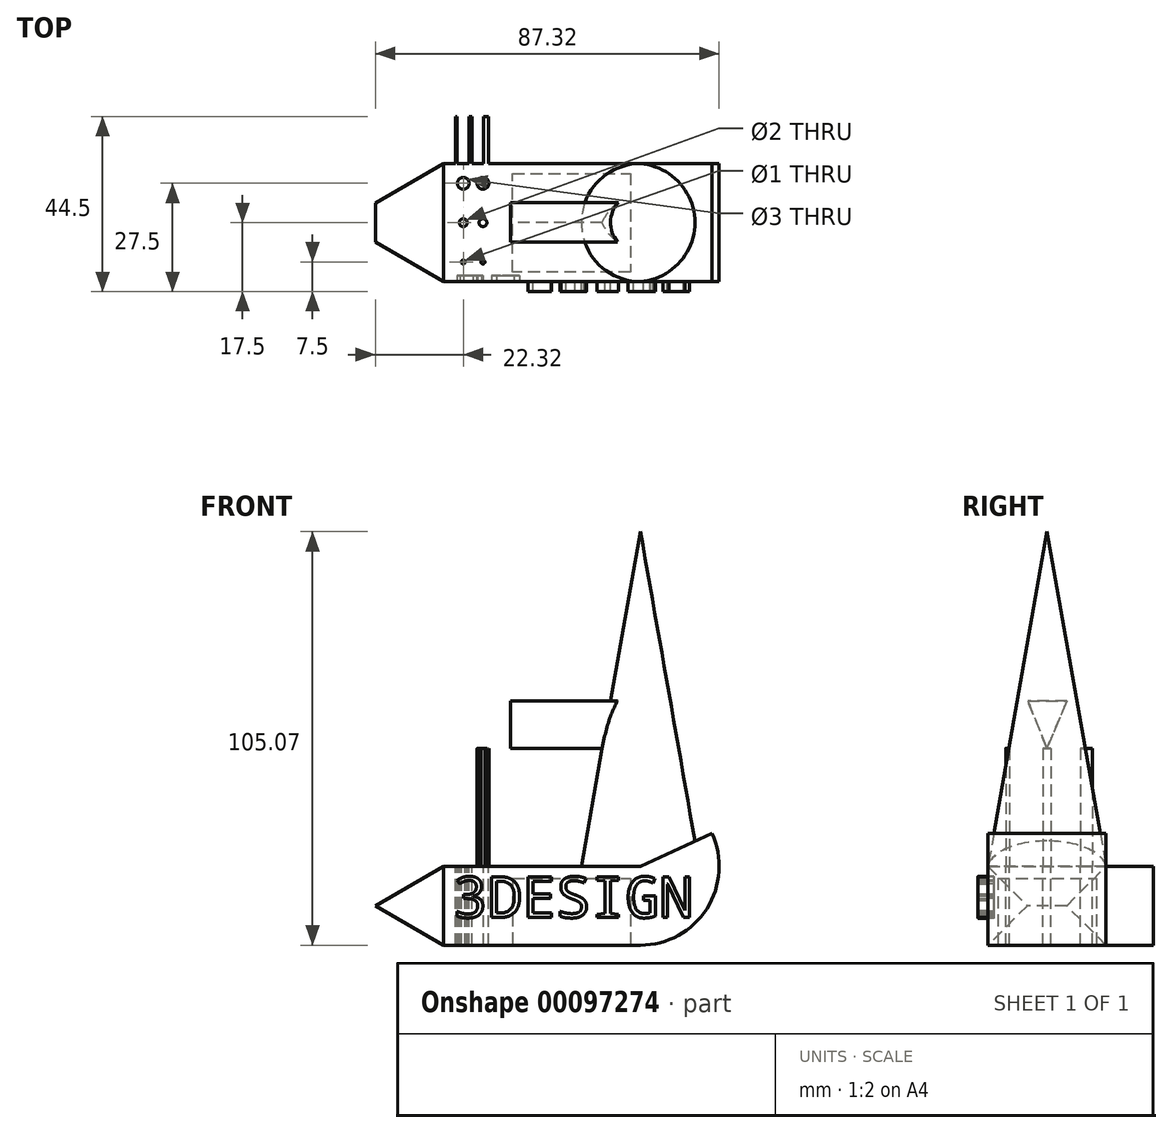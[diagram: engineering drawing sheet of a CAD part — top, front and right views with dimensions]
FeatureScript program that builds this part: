
annotation { "Feature Type Name" : "Feature", "Feature Type Description" : "" }
export const myFeature = defineFeature(function(context is Context, id is Id, definition is map)
    precondition{}
    {
        {
            var Q0;
            Q0=qCreatedBy(makeId("Top.planeOp"),FACE);
            var sketch = newSketch(context, id + "F0", { "sketchPlane" : qUnion([Q0])});
            skLineSegment(sketch, "E0.bottom", {"start": v(25, -15) * mm, "end": v(-25, -15) * mm});
            skLineSegment(sketch, "E0.top", {"start": v(25, 15) * mm, "end": v(-25, 15) * mm});
            skLineSegment(sketch, "E0.left", {"start": v(25, -15) * mm, "end": v(25, 15) * mm});
            skLineSegment(sketch, "E0.right", {"start": v(-25, -15) * mm, "end": v(-25, 15) * mm});
            skPoint(sketch, "E0.middle", {"position": v(0, 0) * mm});
            skSolve(sketch);
        }
        {
            var Q0;
            Q0=makeQuery(id+"F0.imprint","IMPRINT",FACE,{"disambiguationData":[TD([[makeQuery(id+"F0.imprint","IMPRINT",EDGE,{"derivedFrom":sQuery(id+"F0.wireOp",EDGE,"E0.bottom")}),-1.0]])]});
            extrude(context, id + "F1", {"entities" : qUnion([Q0]), "depth" : 20 * mm});
        }
        {
            var Q0;
            Q0=makeQuery(id+"F1.opExtrude","SWEPT_FACE",FACE,{"disambiguationData":[OSD([sQuery(id+"F0.wireOp",EDGE,"E0.bottom")])]});
            var sketch = newSketch(context, id + "F2", { "sketchPlane" : qUnion([Q0])});
            skPoint(sketch, "E1", {"position": v(25, 0) * mm});
            skPoint(sketch, "E2", {"position": v(25, 20) * mm});
            skLineSegment(sketch, "E3", {"start": v(25, 0) * mm, "end": v(25, 20) * mm});
            skLineSegment(sketch, "E4", {"start": v(25, 20) * mm, "end": v(43.13, 28.45) * mm});
            skArc(sketch, "E5", {"start": v(25, 0) * mm, "mid": v(41.87, 9.25) * mm, "end": v(43.13, 28.45) * mm});
            skSolve(sketch);
        }
        {
            var Q0;
            Q0 = qSketchRegion(id + "F2", true);
            var Q1;
            Q1=makeQuery(id+"F1.opExtrude","SWEPT_FACE",FACE,{"disambiguationData":[OSD([sQuery(id+"F0.wireOp",EDGE,"E0.top")])]});
            extrude(context, id + "F3", {"entities" : qUnion([Q0]), "operationType" : NewBodyOperationType.ADD, "endBound" : BoundingType.UP_TO_SURFACE, "oppositeDirection" : true, "endBoundEntityFace" : qUnion([Q1]), "depth" : 25 * mm});
        }
        {
            var Q0;
            Q0=makeQuery(id+"F1.opExtrude","SWEPT_FACE",FACE,{"disambiguationData":[OSD([sQuery(id+"F0.wireOp",EDGE,"E0.right")])]});
            extrude(context, id + "F4", {"entities" : qUnion([Q0]), "operationType" : NewBodyOperationType.ADD, "depth" : 25 * mm, "hasDraft" : true, "draftAngle" : 30 * degree, "draftPullDirection" : true});
        }
        {
            var Q0;
            Q0=makeQuery(id+"F1.opExtrude","CAP_FACE",FACE,{"disambiguationData":[OSD([sQuery(id+"F0.wireOp",EDGE,"E0.bottom"),sQuery(id+"F0.wireOp",EDGE,"E0.top"),sQuery(id+"F0.wireOp",EDGE,"E0.left"),sQuery(id+"F0.wireOp",EDGE,"E0.right")])],"isStart":false});
            var sketch = newSketch(context, id + "F5", { "sketchPlane" : qUnion([Q0])});
            skLineSegment(sketch, "E6", {"start": v(25, 15) * mm, "end": v(25, -15) * mm});
            skCircle(sketch, "E7", {"center": v(25, 0) * mm, "radius": 15 * mm});
            skSolve(sketch);
        }
        {
            var Q0;
            Q0 = qSketchRegion(id + "F5", true);
            extrude(context, id + "F6", {"entities" : qUnion([Q0]), "operationType" : NewBodyOperationType.ADD, "depth" : 90 * mm, "hasDraft" : true, "draftAngle" : 10 * degree, "draftPullDirection" : true});
        }
        {
            var Q0;
            Q0=qCreatedBy(makeId("Right.planeOp"),FACE);
            var sketch = newSketch(context, id + "F7", { "sketchPlane" : qUnion([Q0])});
            skLineSegment(sketch, "E8", {"start": v(0, 20) * mm, "end": v(0, 50) * mm});
            skLineSegment(sketch, "E9", {"start": v(0, 50) * mm, "end": v(-4.88, 62.07) * mm});
            skLineSegment(sketch, "E10", {"start": v(-4.88, 62.07) * mm, "end": v(5.12, 62.07) * mm});
            skLineSegment(sketch, "E11", {"start": v(5.12, 62.07) * mm, "end": v(0, 50) * mm});
            skSolve(sketch);
        }
        {
            var Q0;
            Q0=makeQuery(id+"F7.imprint","IMPRINT",FACE,{"disambiguationData":[TD([[makeQuery(id+"F7.imprint","IMPRINT",EDGE,{"derivedFrom":sQuery(id+"F7.wireOp",EDGE,"E9")}),-1.0]])]});
            extrude(context, id + "F8", {"entities" : qUnion([Q0]), "operationType" : NewBodyOperationType.ADD, "depth" : 25 * mm, "hasSecondDirection" : true, "secondDirectionOppositeDirection" : true, "secondDirectionDepth" : 8 * mm});
        }
        {
            var Q0;
            Q0=makeQuery(id+"F1.opExtrude","CAP_FACE",FACE,{"disambiguationData":[OSD([sQuery(id+"F0.wireOp",EDGE,"E0.bottom"),sQuery(id+"F0.wireOp",EDGE,"E0.top"),sQuery(id+"F0.wireOp",EDGE,"E0.left"),sQuery(id+"F0.wireOp",EDGE,"E0.right")])],"isStart":false});
            var sketch = newSketch(context, id + "F9", { "sketchPlane" : qUnion([Q0])});
            skLineSegment(sketch, "E12", {"start": v(-25, 0) * mm, "end": v(-15, 0) * mm});
            skPoint(sketch, "E12.endSnap0", {"position": v(-25, 0) * mm});
            skCircle(sketch, "E13", {"center": v(-15, 0) * mm, "radius": 1 * mm});
            skCircle(sketch, "E14", {"center": v(-15, -10) * mm, "radius": 0.5 * mm});
            skCircle(sketch, "E15", {"center": v(-15, 10) * mm, "radius": 1.5 * mm});
            skSolve(sketch);
        }
        {
            var Q0;
            Q0 = qSketchRegion(id + "F9", true);
            extrude(context, id + "F10", {"entities" : qUnion([Q0]), "operationType" : NewBodyOperationType.ADD, "depth" : 30 * mm});
        }
        {
            var Q0;
            Q0=makeQuery(id+"F1.opExtrude","CAP_FACE",FACE,{"disambiguationData":[OSD([sQuery(id+"F0.wireOp",EDGE,"E0.bottom"),sQuery(id+"F0.wireOp",EDGE,"E0.top"),sQuery(id+"F0.wireOp",EDGE,"E0.left"),sQuery(id+"F0.wireOp",EDGE,"E0.right")])],"isStart":false});
            var sketch = newSketch(context, id + "F11", { "sketchPlane" : qUnion([Q0])});
            skLineSegment(sketch, "E16", {"start": v(-25, 0) * mm, "end": v(-20, 0) * mm});
            skPoint(sketch, "E16.endSnap0", {"position": v(-25, 0) * mm});
            skCircle(sketch, "E17", {"center": v(-20, 0) * mm, "radius": 1 * mm});
            skCircle(sketch, "E18", {"center": v(-20, -10) * mm, "radius": 0.5 * mm});
            skCircle(sketch, "E19", {"center": v(-20, 10) * mm, "radius": 1.5 * mm});
            skSolve(sketch);
        }
        {
            var Q0;
            Q0 = qSketchRegion(id + "F11", true);
            extrude(context, id + "F12", {"entities" : qUnion([Q0]), "operationType" : NewBodyOperationType.REMOVE, "endBound" : BoundingType.THROUGH_ALL, "oppositeDirection" : true, "depth" : 25 * mm});
        }
        {
            var Q0;
            Q0=makeQuery(id+"F1.opExtrude","CAP_FACE",FACE,{"disambiguationData":[OSD([sQuery(id+"F0.wireOp",EDGE,"E0.bottom"),sQuery(id+"F0.wireOp",EDGE,"E0.top"),sQuery(id+"F0.wireOp",EDGE,"E0.left"),sQuery(id+"F0.wireOp",EDGE,"E0.right")])],"isStart":false});
            var sketch = newSketch(context, id + "F13", { "sketchPlane" : qUnion([Q0])});
            skLineSegment(sketch, "E20", {"start": v(-25, 15) * mm, "end": v(-22, 15) * mm});
            skLineSegment(sketch, "E21", {"start": v(-22, 15) * mm, "end": v(-22, 27) * mm});
            skLineSegment(sketch, "E22", {"start": v(-22, 27) * mm, "end": v(-21.6, 27) * mm});
            skLineSegment(sketch, "E23", {"start": v(-21.6, 27) * mm, "end": v(-21.6, 15) * mm});
            skLineSegment(sketch, "E24", {"start": v(-21.6, 15) * mm, "end": v(-22, 15) * mm});
            skLineSegment(sketch, "E25", {"start": v(-21.6, 15) * mm, "end": v(-18.6, 15) * mm});
            skLineSegment(sketch, "E26", {"start": v(-18.6, 15) * mm, "end": v(-18.6, 27) * mm});
            skLineSegment(sketch, "E27", {"start": v(-18.6, 27) * mm, "end": v(-17.8, 27) * mm});
            skLineSegment(sketch, "E28", {"start": v(-17.8, 27) * mm, "end": v(-17.8, 15) * mm});
            skLineSegment(sketch, "E29", {"start": v(-17.8, 15) * mm, "end": v(-18.6, 15) * mm});
            skLineSegment(sketch, "E30", {"start": v(-17.8, 15) * mm, "end": v(-14.8, 15) * mm});
            skLineSegment(sketch, "E31", {"start": v(-14.8, 15) * mm, "end": v(-14.8, 27) * mm});
            skLineSegment(sketch, "E32", {"start": v(-14.8, 27) * mm, "end": v(-13.6, 27) * mm});
            skLineSegment(sketch, "E33", {"start": v(-13.6, 27) * mm, "end": v(-13.6, 15) * mm});
            skLineSegment(sketch, "E34", {"start": v(-13.6, 15) * mm, "end": v(-14.8, 15) * mm});
            skSolve(sketch);
        }
        {
            var Q0;
            Q0 = qSketchRegion(id + "F13", true);
            extrude(context, id + "F14", {"entities" : qUnion([Q0]), "operationType" : NewBodyOperationType.ADD, "oppositeDirection" : true, "depth" : 20 * mm});
        }
        {
            var Q0;
            Q0=makeQuery(id+"F14.boolean.opBoolean","MERGE",FACE,{"derivedFrom":[makeQuery(id+"F1.opExtrude","CAP_FACE",FACE,{"disambiguationData":[OSD([sQuery(id+"F0.wireOp",EDGE,"E0.bottom"),sQuery(id+"F0.wireOp",EDGE,"E0.top"),sQuery(id+"F0.wireOp",EDGE,"E0.left"),sQuery(id+"F0.wireOp",EDGE,"E0.right")])],"isStart":true}),makeQuery(id+"F14.opExtrude","CAP_FACE",FACE,{"disambiguationData":[OSD([sQuery(id+"F13.wireOp",EDGE,"E21"),sQuery(id+"F13.wireOp",EDGE,"E22"),sQuery(id+"F13.wireOp",EDGE,"E23"),sQuery(id+"F13.wireOp",EDGE,"E24")])],"isStart":false}),makeQuery(id+"F14.opExtrude","CAP_FACE",FACE,{"disambiguationData":[OSD([sQuery(id+"F13.wireOp",EDGE,"E26"),sQuery(id+"F13.wireOp",EDGE,"E27"),sQuery(id+"F13.wireOp",EDGE,"E28"),sQuery(id+"F13.wireOp",EDGE,"E29")])],"isStart":false}),makeQuery(id+"F14.opExtrude","CAP_FACE",FACE,{"disambiguationData":[OSD([sQuery(id+"F13.wireOp",EDGE,"E31"),sQuery(id+"F13.wireOp",EDGE,"E32"),sQuery(id+"F13.wireOp",EDGE,"E33"),sQuery(id+"F13.wireOp",EDGE,"E34")])],"isStart":false})]});
            var sketch = newSketch(context, id + "F15", { "sketchPlane" : qUnion([Q0])});
            skLineSegment(sketch, "E35", {"start": v(0, 15) * mm, "end": v(0, 12.5) * mm});
            skLineSegment(sketch, "E36", {"start": v(25, 0) * mm, "end": v(22.5, 0) * mm});
            skPoint(sketch, "E36.endSnap0", {"position": v(25, 0) * mm});
            skLineSegment(sketch, "E37", {"start": v(22.5, 0) * mm, "end": v(22.5, 12.5) * mm});
            skLineSegment(sketch, "E38", {"start": v(22.5, 12.5) * mm, "end": v(-7.5, 12.5) * mm});
            skLineSegment(sketch, "E39", {"start": v(0, -15) * mm, "end": v(0, -12.5) * mm});
            skLineSegment(sketch, "E40", {"start": v(-7.5, 12.5) * mm, "end": v(-7.5, -12.5) * mm});
            skLineSegment(sketch, "E41", {"start": v(-7.5, -12.5) * mm, "end": v(22.5, -12.5) * mm});
            skLineSegment(sketch, "E42", {"start": v(22.5, -12.5) * mm, "end": v(22.5, 0) * mm});
            skSolve(sketch);
        }
        {
            var Q0;
            Q0 = qSketchRegion(id + "F15", true);
            extrude(context, id + "F16", {"entities" : qUnion([Q0]), "operationType" : NewBodyOperationType.REMOVE, "oppositeDirection" : true, "depth" : 17 * mm});
        }
        {
            var Q0;
            Q0=makeQuery(id+"F3.boolean.opBoolean","MERGE",FACE,{"derivedFrom":[makeQuery(id+"F1.opExtrude","SWEPT_FACE",FACE,{"disambiguationData":[OSD([sQuery(id+"F0.wireOp",EDGE,"E0.bottom")])]}),makeQuery(id+"F3.opExtrude","CAP_FACE",FACE,{"disambiguationData":[OSD([sQuery(id+"F2.wireOp",EDGE,"E3"),sQuery(id+"F2.wireOp",EDGE,"E4"),sQuery(id+"F2.wireOp",EDGE,"E5")])],"isStart":true})]});
            var sketch = newSketch(context, id + "F17", { "sketchPlane" : qUnion([Q0])});
            skText(sketch, "E43", { "text": "3DESIGN", "fontName": "DroidSansMono.ttf"});
            const initialGuessF17  = {"E43": [-0.0225, 0.007, 1, 0, 0.01045]};
            skSetInitialGuess(sketch, initialGuessF17);
            skSolve(sketch);
        }
        {
            var Q0;
            Q0 = qSketchRegion(id + "F17", true);
            extrude(context, id + "F18", {"entities" : qUnion([Q0]), "operationType" : NewBodyOperationType.ADD, "depth" : 2.5 * mm});
        }
        {
            var Q0;
            Q0=makeQuery(id+"F18.opExtrude","CAP_FACE",FACE,{"disambiguationData":[OSD([sQuery(id+"F17.wireOp",EDGE,"E43.sketch_text.stroke-0"),sQuery(id+"F17.wireOp",EDGE,"E43.sketch_text.stroke-1"),sQuery(id+"F17.wireOp",EDGE,"E43.sketch_text.stroke-2"),sQuery(id+"F17.wireOp",EDGE,"E43.sketch_text.stroke-3"),sQuery(id+"F17.wireOp",EDGE,"E43.sketch_text.stroke-4"),sQuery(id+"F17.wireOp",EDGE,"E43.sketch_text.stroke-5"),sQuery(id+"F17.wireOp",EDGE,"E43.sketch_text.stroke-6"),sQuery(id+"F17.wireOp",EDGE,"E43.sketch_text.stroke-7"),sQuery(id+"F17.wireOp",EDGE,"E43.sketch_text.stroke-8"),sQuery(id+"F17.wireOp",EDGE,"E43.sketch_text.stroke-9"),sQuery(id+"F17.wireOp",EDGE,"E43.sketch_text.stroke-10"),sQuery(id+"F17.wireOp",EDGE,"E43.sketch_text.stroke-11"),sQuery(id+"F17.wireOp",EDGE,"E43.sketch_text.stroke-12"),sQuery(id+"F17.wireOp",EDGE,"E43.sketch_text.stroke-13"),sQuery(id+"F17.wireOp",EDGE,"E43.sketch_text.stroke-14"),sQuery(id+"F17.wireOp",EDGE,"E43.sketch_text.stroke-15"),sQuery(id+"F17.wireOp",EDGE,"E43.sketch_text.stroke-16"),sQuery(id+"F17.wireOp",EDGE,"E43.sketch_text.stroke-17"),sQuery(id+"F17.wireOp",EDGE,"E43.sketch_text.stroke-18"),sQuery(id+"F17.wireOp",EDGE,"E43.sketch_text.stroke-19"),sQuery(id+"F17.wireOp",EDGE,"E43.sketch_text.stroke-20"),sQuery(id+"F17.wireOp",EDGE,"E43.sketch_text.stroke-21"),sQuery(id+"F17.wireOp",EDGE,"E43.sketch_text.stroke-22")])],"isStart":false});
            var Q1;
            Q1=makeQuery(id+"F18.opExtrude","CAP_FACE",FACE,{"disambiguationData":[OSD([sQuery(id+"F17.wireOp",EDGE,"E43.sketch_text.stroke-23"),sQuery(id+"F17.wireOp",EDGE,"E43.sketch_text.stroke-24"),sQuery(id+"F17.wireOp",EDGE,"E43.sketch_text.stroke-25"),sQuery(id+"F17.wireOp",EDGE,"E43.sketch_text.stroke-26"),sQuery(id+"F17.wireOp",EDGE,"E43.sketch_text.stroke-27"),sQuery(id+"F17.wireOp",EDGE,"E43.sketch_text.stroke-28"),sQuery(id+"F17.wireOp",EDGE,"E43.sketch_text.stroke-29"),sQuery(id+"F17.wireOp",EDGE,"E43.sketch_text.stroke-30"),sQuery(id+"F17.wireOp",EDGE,"E43.sketch_text.stroke-31"),sQuery(id+"F17.wireOp",EDGE,"E43.sketch_text.stroke-32"),sQuery(id+"F17.wireOp",EDGE,"E43.sketch_text.stroke-33"),sQuery(id+"F17.wireOp",EDGE,"E43.sketch_text.stroke-34")])],"isStart":false});
            extrude(context, id + "F19", {"entities" : qUnion([Q0, Q1]), "operationType" : NewBodyOperationType.REMOVE, "oppositeDirection" : true, "depth" : 4 * mm});
        }
    });
